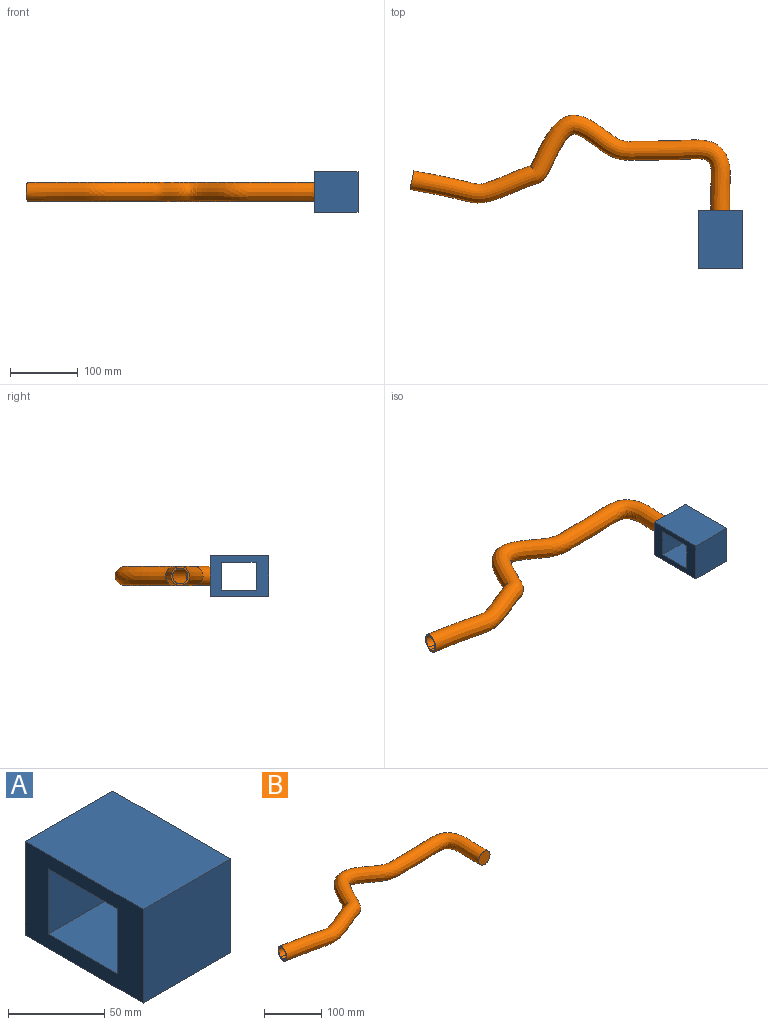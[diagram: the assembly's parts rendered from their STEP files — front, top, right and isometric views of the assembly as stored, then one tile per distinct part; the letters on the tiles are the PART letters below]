
ASSEMBLY  parts=2 mates=1
PART A: 10 faces, bbox 64x86.2x59.4 mm
  f0: plane 86.23x59.44mm, normal (-1,0,0), area 3028.1mm2, adj f2,f3,f4,f5,f6,f7,f8,f9
  f1: plane 86.23x59.44mm, normal (1,0,0), area 3028.1mm2, adj f2,f3,f4,f5,f6,f7,f8,f9
  f2: plane 64.04x59.44mm, normal (0,-1,0), area 3806.2mm2, adj f0,f1,f4,f5
  f3: plane 64.04x59.44mm, normal (0,1,0), area 3806.2mm2, adj f0,f1,f4,f5
  f4: plane 86.23x64.04mm, normal (0,0,1), area 5522.1mm2, adj f0,f1,f2,f3
  f5: plane 86.23x64.04mm, normal (0,0,-1), area 5522.1mm2, adj f0,f1,f2,f3
  f6: plane 64.04x50.73mm, normal (0,0,-1), area 3248.6mm2, adj f0,f1,f7,f9
  f7: plane 64.04x41.34mm, normal (0,1,0), area 2647.3mm2, adj f0,f1,f6,f8
  f8: plane 64.04x50.73mm, normal (0,0,1), area 3248.6mm2, adj f0,f1,f7,f9
  f9: plane 64.04x41.34mm, normal (0,-1,0), area 2647.3mm2, adj f0,f1,f6,f8
PART B: 8 faces, bbox 495.5x163.2x33.2 mm
  f0: plane 32.04x31.47mm, normal (-0.98,0.2,0), area 204.2mm2, adj f2,f3,f6
  f1: plane 32.04x32.04mm, normal (0,-1,0), area 621.3mm2, adj f2
  f2: bspline ~490.47x158.15mm, area 52200mm2, adj f0,f1
  f3: offset ~467.93x135.05mm, area 3150.7mm2, adj f0,f4,f5,f6,f7
  f4: offset ~289.78x142.61mm, area 10069.8mm2, adj f3,f5,f7
  f5: bspline ~39.3x35.67mm, area 1291.5mm2, adj f3,f4,f6
  f6: offset ~160.08x32.14mm, area 4089.8mm2, adj f0,f3,f5
  f7: plane 24.17x24.17mm, normal (0,1,0), area 417.2mm2, adj f3,f4
PLACE A at identity
PLACE B t=(-7.18,33.64,29.72)mm
MATE slider B.f1 <-> A.f3  axis (0,-1,0) through (-7.18,33.64,29.72)mm
